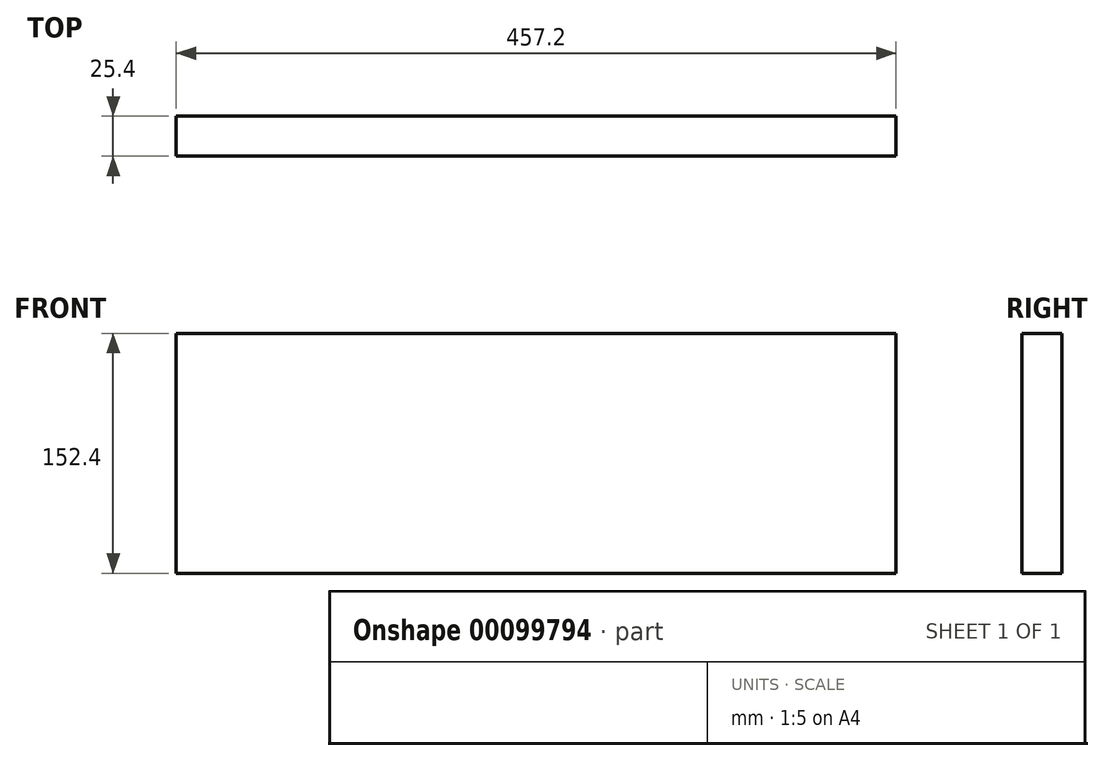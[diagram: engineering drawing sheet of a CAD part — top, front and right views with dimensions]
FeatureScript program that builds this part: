
annotation { "Feature Type Name" : "Feature", "Feature Type Description" : "" }
export const myFeature = defineFeature(function(context is Context, id is Id, definition is map)
    precondition{}
    {
        {
            var Q0;
            Q0=qCreatedBy(makeId("Front.planeOp"),FACE);
            var sketch = newSketch(context, id + "F0", { "sketchPlane" : qUnion([Q0])});
            skLineSegment(sketch, "E0.bottom", {"start": v(-236.09, -105.06) * mm, "end": v(221.11, -105.06) * mm});
            skLineSegment(sketch, "E0.top", {"start": v(-236.09, 47.34) * mm, "end": v(221.11, 47.34) * mm});
            skLineSegment(sketch, "E0.left", {"start": v(-236.09, -105.06) * mm, "end": v(-236.09, 47.34) * mm});
            skLineSegment(sketch, "E0.right", {"start": v(221.11, -105.06) * mm, "end": v(221.11, 47.34) * mm});
            skSolve(sketch);
        }
        {
            var Q0;
            Q0=makeQuery(id+"F0.imprint","IMPRINT",FACE,{"disambiguationData":[TD([[makeQuery(id+"F0.imprint","IMPRINT",EDGE,{"derivedFrom":sQuery(id+"F0.wireOp",EDGE,"E0.bottom")}),1.0]])]});
            extrude(context, id + "F1", {"entities" : qUnion([Q0]), "depth" : 25.4 * mm});
        }
    });
